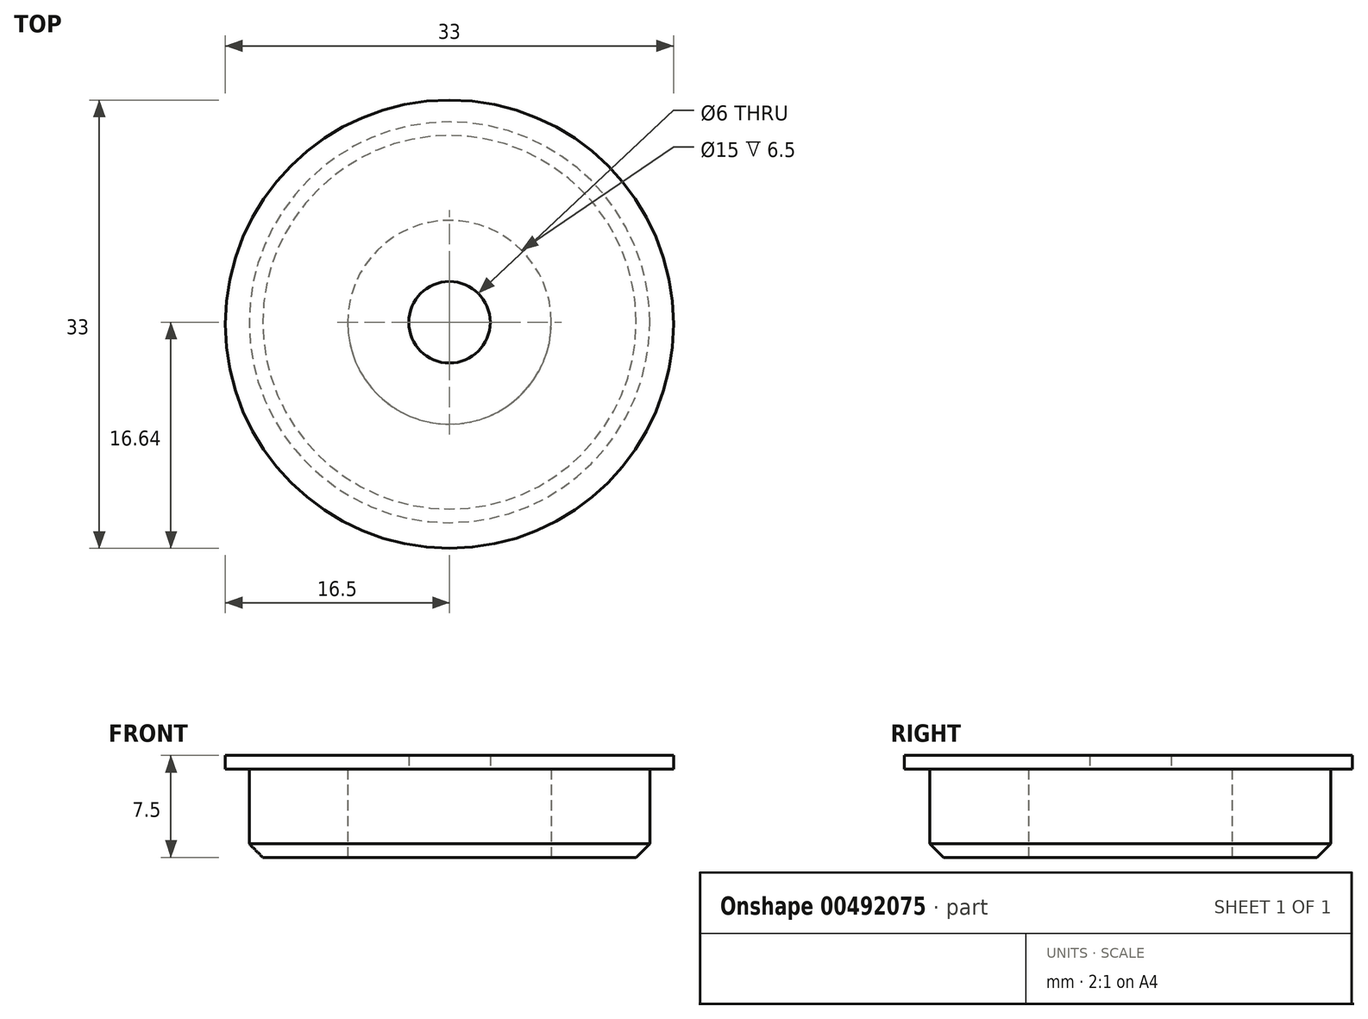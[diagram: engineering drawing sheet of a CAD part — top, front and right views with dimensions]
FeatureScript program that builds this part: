
annotation { "Feature Type Name" : "Feature", "Feature Type Description" : "" }
export const myFeature = defineFeature(function(context is Context, id is Id, definition is map)
    precondition{}
    {
        {
            var Q0;
            Q0=qCreatedBy(makeId("Top.planeOp"),FACE);
            var sketch = newSketch(context, id + "F0", { "sketchPlane" : qUnion([Q0])});
            skCircle(sketch, "E0", {"center": v(0, -0.14) * mm, "radius": 16.5 * mm});
            skSolve(sketch);
        }
        {
            var Q0;
            Q0=makeQuery(id+"F0.imprint","IMPRINT",FACE,{"disambiguationData":[TD([[makeQuery(id+"F0.imprint","IMPRINT",EDGE,{"derivedFrom":sQuery(id+"F0.wireOp",EDGE,"E0")}),1.0]])]});
            extrude(context, id + "F1", {"entities" : qUnion([Q0]), "depth" : 1 * mm});
        }
        {
            var Q0;
            Q0=makeQuery(id+"F1.opExtrude","CAP_FACE",FACE,{"disambiguationData":[OSD([sQuery(id+"F0.wireOp",EDGE,"E0")])],"isStart":true});
            var sketch = newSketch(context, id + "F2", { "sketchPlane" : qUnion([Q0])});
            skCircle(sketch, "E1", {"center": v(0, 0) * mm, "radius": 14.75 * mm});
            skSolve(sketch);
        }
        {
            var Q0;
            Q0 = qSketchRegion(id + "F2", true);
            extrude(context, id + "F3", {"entities" : qUnion([Q0]), "operationType" : NewBodyOperationType.ADD, "depth" : 6.5 * mm});
        }
        {
            var Q0;
            Q0=makeQuery(id+"F3.opExtrude","CAP_FACE",FACE,{"disambiguationData":[OSD([sQuery(id+"F2.wireOp",EDGE,"E1")])],"isStart":false});
            var sketch = newSketch(context, id + "F4", { "sketchPlane" : qUnion([Q0])});
            skCircle(sketch, "E2", {"center": v(0, 0) * mm, "radius": 3 * mm});
            skSolve(sketch);
        }
        {
            var Q0;
            Q0 = qSketchRegion(id + "F4", true);
            extrude(context, id + "F5", {"entities" : qUnion([Q0]), "operationType" : NewBodyOperationType.REMOVE, "oppositeDirection" : true, "depth" : 25 * mm});
        }
        {
            var Q0;
            Q0=makeQuery(id+"F4.imprint","IMPRINT",FACE,{"disambiguationData":[TD([[makeQuery(id+"F4.imprint","IMPRINT",EDGE,{"derivedFrom":sQuery(id+"F4.wireOp",EDGE,"E2")}),-1.0]])]});
            var sketch = newSketch(context, id + "F6", { "sketchPlane" : qUnion([Q0])});
            skCircle(sketch, "E3", {"center": v(0, 0) * mm, "radius": 7.5 * mm});
            skSolve(sketch);
        }
        {
            var Q0;
            Q0 = qSketchRegion(id + "F6", true);
            var Q1;
            Q1=qCreatedBy(makeId("Top.planeOp"),FACE);
            extrude(context, id + "F7", {"entities" : qUnion([Q0]), "operationType" : NewBodyOperationType.REMOVE, "endBound" : BoundingType.UP_TO_SURFACE, "oppositeDirection" : true, "endBoundEntityFace" : qUnion([Q1]), "depth" : 25 * mm});
        }
        {
            var Q0;
            Q0=makeQuery(id+"F7.boolean.opBoolean","COPY",EDGE,{"derivedFrom":makeQuery(id+"F7.opExtrude","CAP_EDGE",EDGE,{"disambiguationData":[OSD([sQuery(id+"F6.wireOp",EDGE,"E3")])],"isStart":true})});
            var Q1;
            Q1=makeQuery(id+"F3.opExtrude","CAP_EDGE",EDGE,{"disambiguationData":[OSD([sQuery(id+"F2.wireOp",EDGE,"E1")])],"isStart":false});
            chamfer(context, id + "F8", {"entities" : qUnion([Q0, Q1]), "width" : 1 * mm, "tangentPropagation" : true});
        }
    });
